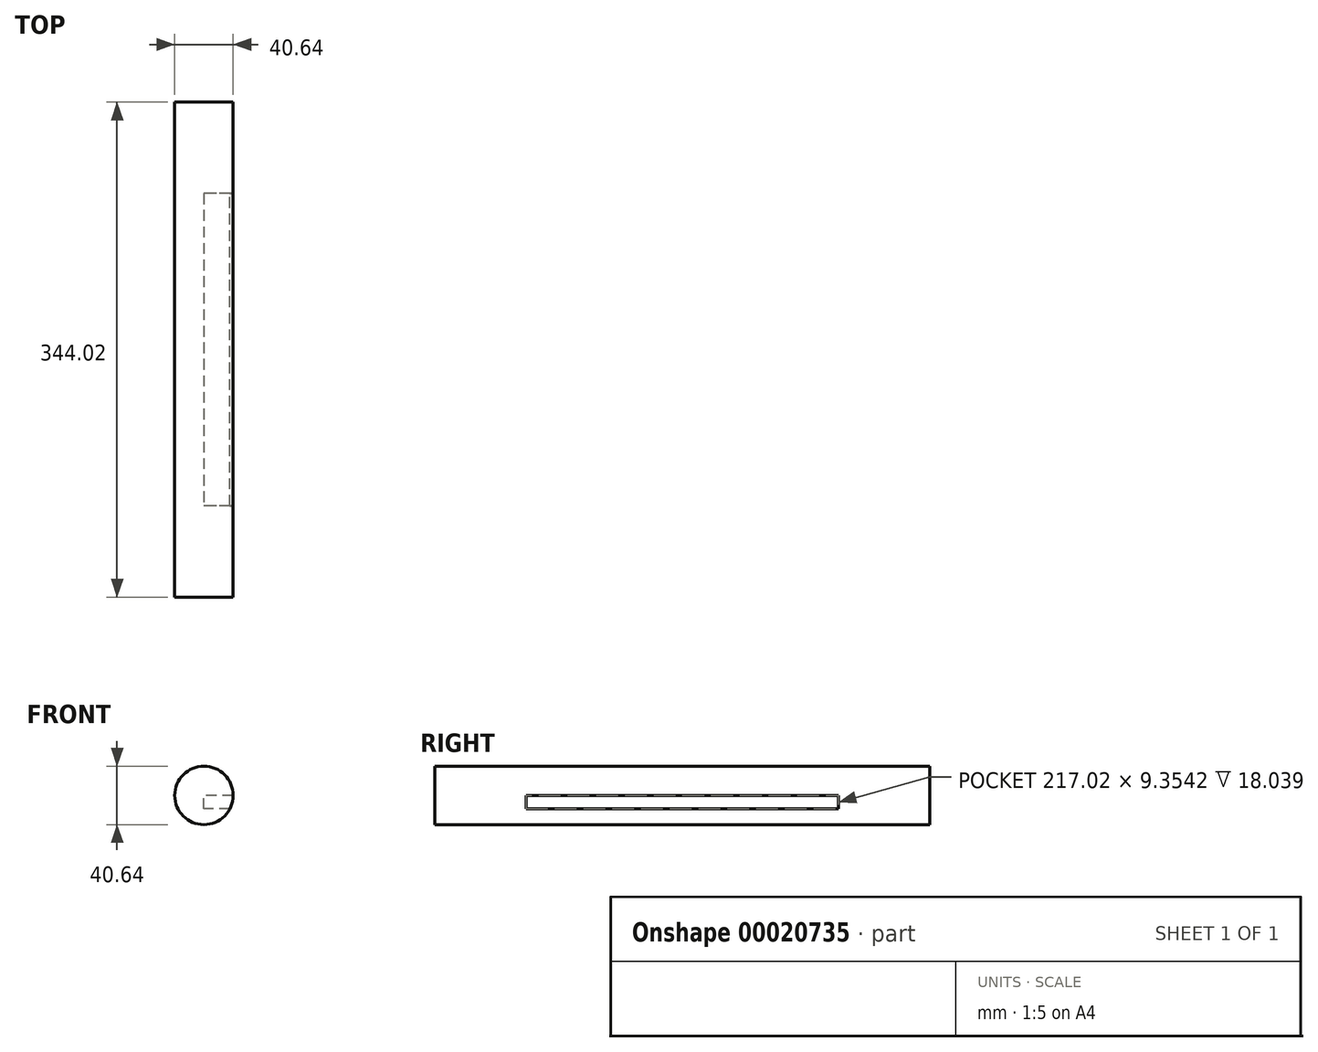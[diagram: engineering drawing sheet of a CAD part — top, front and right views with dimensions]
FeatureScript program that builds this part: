
annotation { "Feature Type Name" : "Feature", "Feature Type Description" : "" }
export const myFeature = defineFeature(function(context is Context, id is Id, definition is map)
    precondition{}
    {
        {
            var Q0;
            Q0=qCreatedBy(makeId("Front.planeOp"),FACE);
            var sketch = newSketch(context, id + "F0", { "sketchPlane" : qUnion([Q0])});
            skCircle(sketch, "E0", {"center": v(0, 0) * mm, "radius": 20.32 * mm});
            skSolve(sketch);
        }
        {
            var Q0;
            Q0 = qSketchRegion(id + "F0", true);
            extrude(context, id + "F1", {"entities" : qUnion([Q0]), "depth" : 344.02 * mm});
        }
        {
            var Q0;
            Q0=qCreatedBy(makeId("Right.planeOp"),FACE);
            var sketch = newSketch(context, id + "F2", { "sketchPlane" : qUnion([Q0])});
            skLineSegment(sketch, "E1.bottom", {"start": v(-63.5, -9.35) * mm, "end": v(-280.52, -9.35) * mm});
            skLineSegment(sketch, "E1.top", {"start": v(-63.5, 0) * mm, "end": v(-280.52, 0) * mm});
            skLineSegment(sketch, "E1.left", {"start": v(-63.5, -9.35) * mm, "end": v(-63.5, 0) * mm});
            skLineSegment(sketch, "E1.right", {"start": v(-280.52, -9.35) * mm, "end": v(-280.52, 0) * mm});
            skSolve(sketch);
        }
        {
            var Q0;
            Q0 = qSketchRegion(id + "F2", true);
            extrude(context, id + "F3", {"entities" : qUnion([Q0]), "operationType" : NewBodyOperationType.REMOVE, "endBound" : BoundingType.THROUGH_ALL, "depth" : 12.4 * mm});
        }
    });
